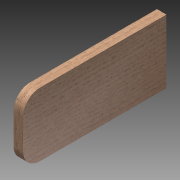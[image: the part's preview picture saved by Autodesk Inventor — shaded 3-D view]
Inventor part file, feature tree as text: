
AUTODESK INVENTOR PART (.ipt)
format: ipt  version: 2014 SP1 (Build 180222100, 222)  size: 101,376 bytes
history: native  units: in
note: dims shown in document units (in); Inventor stores cm internally (conversion verified against a paired STEP export)
features: extrude x1, fillet x1, sketch x1
ambient origin geometry x8: Origin, YZ Plane, XZ Plane, XY Plane, X Axis, Y Axis, Z Axis, Center Point
bodies: Solid1 (feature_tree)
feature tree (3):
  extrude  "Extrusion1"  Depth=0.75in
  fillet  "Fillet1"  Radius=11.25in
  sketch  "Sketch1"  dims[d0=5.0in d1=0.75in d2=11.25in d3=0.0in d4=1.3125in]
